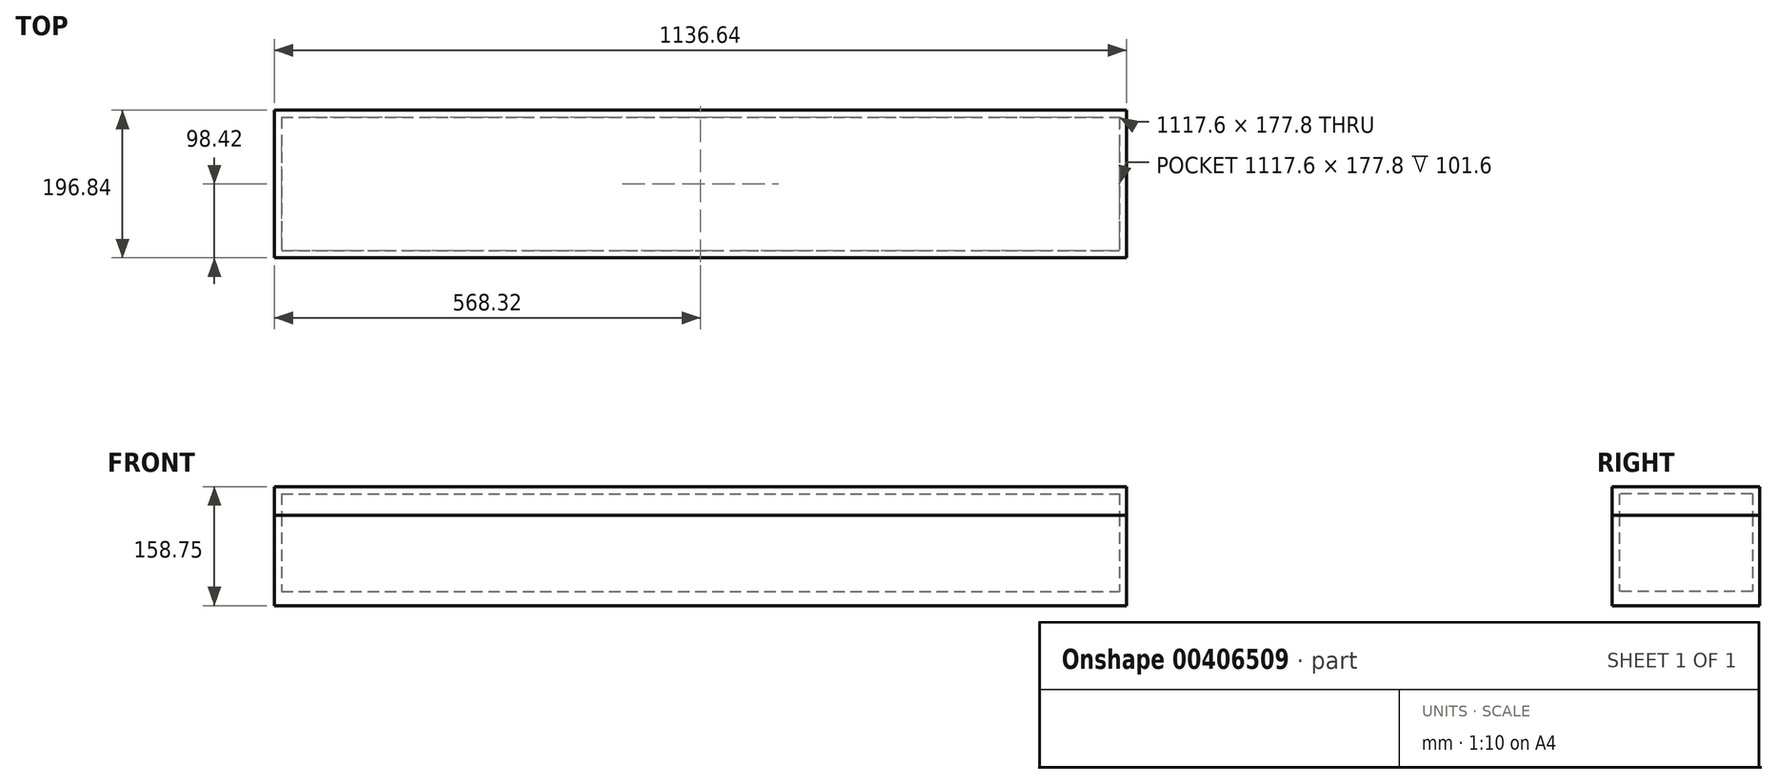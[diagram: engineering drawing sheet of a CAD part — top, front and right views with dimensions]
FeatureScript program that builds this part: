
annotation { "Feature Type Name" : "Feature", "Feature Type Description" : "" }
export const myFeature = defineFeature(function(context is Context, id is Id, definition is map)
    precondition{}
    {
        {
            var Q0;
            Q0=qCreatedBy(makeId("Top.planeOp"),FACE);
            var sketch = newSketch(context, id + "F0", { "sketchPlane" : qUnion([Q0])});
            skLineSegment(sketch, "E0.bottom", {"start": v(-568.33, 98.42) * mm, "end": v(568.33, 98.42) * mm});
            skLineSegment(sketch, "E0.top", {"start": v(-568.33, -98.42) * mm, "end": v(568.33, -98.42) * mm});
            skLineSegment(sketch, "E0.left", {"start": v(-568.33, 98.42) * mm, "end": v(-568.33, -98.43) * mm});
            skLineSegment(sketch, "E0.right", {"start": v(568.33, 98.42) * mm, "end": v(568.33, -98.42) * mm});
            skPoint(sketch, "E0.middle", {"position": v(0, 0) * mm});
            skLineSegment(sketch, "E1.bottom", {"start": v(558.8, 88.9) * mm, "end": v(-558.8, 88.9) * mm});
            skLineSegment(sketch, "E1.top", {"start": v(558.8, -88.9) * mm, "end": v(-558.8, -88.9) * mm});
            skLineSegment(sketch, "E1.left", {"start": v(558.8, 88.9) * mm, "end": v(558.8, -88.9) * mm});
            skLineSegment(sketch, "E1.right", {"start": v(-558.8, 88.9) * mm, "end": v(-558.8, -88.9) * mm});
            skSolve(sketch);
        }
        {
            var Q0;
            Q0=makeQuery(id+"F0.imprint","IMPRINT",FACE,{"disambiguationData":[TD([[makeQuery(id+"F0.imprint","IMPRINT",EDGE,{"derivedFrom":sQuery(id+"F0.wireOp",EDGE,"E1.bottom")}),1.0]])]});
            var Q1;
            Q1=makeQuery(id+"F0.imprint","IMPRINT",FACE,{"disambiguationData":[TD([[makeQuery(id+"F0.imprint","IMPRINT",EDGE,{"derivedFrom":sQuery(id+"F0.wireOp",EDGE,"E0.bottom")}),-1.0]])]});
            extrude(context, id + "F1", {"entities" : qUnion([Q0, Q1]), "depth" : 111.12 * mm, "offsetDistance" : 25.4 * mm});
        }
        {
            var Q0;
            Q0=makeQuery(id+"F1.opExtrude","CAP_FACE",FACE,{"disambiguationData":[OSD([sQuery(id+"F0.wireOp",EDGE,"E0.bottom"),sQuery(id+"F0.wireOp",EDGE,"E0.top"),sQuery(id+"F0.wireOp",EDGE,"E0.left"),sQuery(id+"F0.wireOp",EDGE,"E0.right")])],"isStart":false});
            extrude(context, id + "F2", {"entities" : qUnion([Q0]), "depth" : 38.1 * mm, "offsetDistance" : 25.4 * mm});
        }
        {
            var Q0;
            Q0=makeQuery(id+"F1.opExtrude","CAP_FACE",FACE,{"disambiguationData":[OSD([sQuery(id+"F0.wireOp",EDGE,"E0.bottom"),sQuery(id+"F0.wireOp",EDGE,"E0.top"),sQuery(id+"F0.wireOp",EDGE,"E0.left"),sQuery(id+"F0.wireOp",EDGE,"E0.right")])],"isStart":false});
            var Q1;
            Q1=makeQuery(id+"F2.opExtrude","CAP_FACE",FACE,{"disambiguationData":[OSD([sQuery(id+"F0.wireOp",EDGE,"E0.bottom"),sQuery(id+"F0.wireOp",EDGE,"E0.top"),sQuery(id+"F0.wireOp",EDGE,"E0.left"),sQuery(id+"F0.wireOp",EDGE,"E0.right")])],"isStart":true});
            shell(context, id + "F3", {"entities" : qUnion([Q0, Q1]), "thickness" : 9.52 * mm});
        }
        {
            var Q0;
            Q0=makeQuery(id+"F0.imprint","IMPRINT",FACE,{"disambiguationData":[TD([[makeQuery(id+"F0.imprint","IMPRINT",EDGE,{"derivedFrom":sQuery(id+"F0.wireOp",EDGE,"E1.bottom")}),1.0]])]});
            var Q1;
            Q1=makeQuery(id+"F0.imprint","IMPRINT",FACE,{"disambiguationData":[TD([[makeQuery(id+"F0.imprint","IMPRINT",EDGE,{"derivedFrom":sQuery(id+"F0.wireOp",EDGE,"E0.bottom")}),-1.0]])]});
            extrude(context, id + "F4", {"entities" : qUnion([Q0, Q1]), "operationType" : NewBodyOperationType.ADD, "oppositeDirection" : true, "depth" : 9.52 * mm, "offsetDistance" : 25.4 * mm});
        }
    });
